# Revit family: 05-E090-DC-CL
name_source: partatom
category: Luminarias
revit_build: Autodesk Revit 2017 (Build: 20160225_1515(x64)
units: mm (PartAtom-declared; Revit-internal decimal feet)

## family parameters
Anfitrión = Cara
Compartido = Sí
Corte con vacíos al cargar = No
Cota de conector redondo = Diámetro de uso
Número OmniClass = 23.80.70.00
Origen de luz = No
Punto de cálculo de habitación = No
Tipo de pieza = Normal
Título OmniClass = Lighting

## types (1)
- 05-E090-DC-CL
    Acabado = Cemento, Gris urbano, Arenado
    CRI = 80
    Carga aparente = 0 VA
    Catálogo = Outdoor
    CodigoGubimclass = 50.60.50.20
    CodigoOmniclass = 21-04 50 40
    CodigoUniclass2015 = EF_70_80
    CodigoUniformat2010 = D5040
    DescripcionGubimclass = Iluminación interior
    DescripcionOmniclass = Lighting
    DescripcionUniclass2015 = Lighting
    DescripcionUniformat2010 = Lighting
    EAN13 = 8435575319264
    Eficiencia energética = LED A++
    Elevación por defecto = 1000 mm  [stored 3.28084 ft]
    Etiqueta V/f = 230V/50-60Hz
    Fabricante = LEDS C4
    Familia = Arc
    FechaVersion = Julio 2020
    Ficha = http://files.leds-c4.com
    Fotometría = http://files.leds-c4.com
    IK = IK10
    IMC = http://files.leds-c4.com
    IP = IP65
    IfcExportAs = IfcLightFixture
IfcLightFixture
    IfcExportType = NOTDEFINED
    Imagen web = http://files.leds-c4.com
    LDT = http://files.leds-c4.com
    Lumenes reales (lm) = 404
    Material = Cemento, Aluminio, Cristal
    Peso neto (KG) = 3.2
    Producto descatalogado = Catalogado ES
    Rayo de luz = Check Photometric file
    Referencia = 05-E090-DC-CL
    Temperatura color led (K) = Blanco cálido - 3000K
    Tender text (Castellano) = LEDS C4
Arc
05-E090-DC-CL

Empotrado de pared de uso interior y exterior para iluminar frontalmente y hacia abajo. 
Apto para instalar en ambientes con atmósfera marina. Incluye 2 salidas de cable para facilitar la instalación en cadena. Material estructura: Cemento, Aluminio. Acabado estructura: Cemento, Gris urbano. Material difusor: Cristal. Acabado difusor: Arenado. Protección contra los rayos ultravioleta. Garantía: 5 Años.

Peso neto del producto (Kg): 3.200
Longitud del producto (mm): 300
Altura del producto (mm): 140
Salida del producto (mm): 63
Ø del agujero para empotrar (mm): 300x140

Clase 1. IP: IP65. IK: IK10. LED. Nº de portalámparas o Leds: 26. Marca del LED: HONGLITRONIC. Marca del Driver: DRIVER AC. Potencia máxima de la fuente de luz: 9W. Temperatura de color: Blanco cálido - 3000K. Índice de reproducción cromática: 80. Steps Mac Adam: 3. Diámetro máximo de la bombilla que admite la luminaria: 50.000h L80B20. UGR:  18.9. Riesgo fotobiológico: RG0. Flujo real (lm): 404. Lm/W reales: 45. Rango de voltaje/frecuencia: 220-240/50-60Hz. Voltaje: 9. Equipo incluido: Si, electrónico. Potencia total: 9.
    Tender text (English) = LEDS C4
Arc
05-E090-DC-CL

Wall recessed for indoor and outdoor use. 

For frontal lighting and downlighting. Suitable for installation in marine environments. Includes 2 cable outlets to facilitate chain mounting. Structure material: cement, Aluminium. Structure finish: Cement, Urban grey. Diffuser material: Glass. Diffuser finish: Sandblasted. UV protection. Warranty: 5 Years.

Product net weight (Kg): 3.200
Product length (mm): 300
Product height (mm): 140
Product aperture (mm): 63
Ø of the hole for recessing (mm): 300x140

Class 1. IP: IP65. IK: IK10. LED. No. of lampholders or LEDs: 26. LED brand: HONGLITRONIC. Driver brand: DRIVER AC. Maximum power of light source: 9W. Colour temperature: LED warm-white 3000K. Colour rendering index: 80. MacAdam Steps: 3. Maximum diameter of luminaire bulb: 50.000h L80B20. UGR:  18.9. Photobiological risk: RG0. Real flux (lm): 404. Lm/Real W: 45. Voltage and frequency range: 220-240/50-60Hz. Voltage: 9. Gear included: Yes, electronic. Total power: 9.
    Tipo = Empotrable de pared
    Vatios (W) = 9
    Versión = v1

note: [stored X ft] marks values corroborated as IEEE doubles in the binary element streams (Revit-internal decimal feet)
